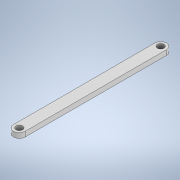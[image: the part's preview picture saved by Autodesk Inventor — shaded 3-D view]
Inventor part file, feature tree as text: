
AUTODESK INVENTOR PART (.ipt)
format: ipt  version: 2020 (Build 240168000, 168)  size: 112,640 bytes
history: native  units: in
note: dims shown in document units (in); Inventor stores cm internally (conversion verified against a paired STEP export)
features: extrude x2, sketch x2
ambient origin geometry x8: Origin, YZ Plane, XZ Plane, XY Plane, X Axis, Y Axis, Z Axis, Center Point
bodies: Solid1 (feature_tree)
feature tree (4):
  extrude  "Extrusion1"  Depth=0.2756in
  extrude  "Extrusion2"  Depth=3.3465in
  sketch  "Sketch1"  dims[d0=0.2756in d1=0.2756in]
  sketch  "Sketch2"  dims[d2=0.1181in d3=0.0in d4=0.1575in d5=0.1575in d7=0.1181in d8=0.0in d9=3.3465in d10=0.0591in]
